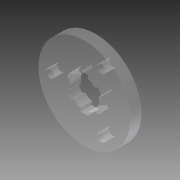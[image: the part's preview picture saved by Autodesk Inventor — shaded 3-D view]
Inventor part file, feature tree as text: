
AUTODESK INVENTOR PART (.ipt)
format: ipt  version: 2014 SP1 (Build 180222100, 222)  size: 126,976 bytes
history: native  units: in
note: dims shown in document units (in); Inventor stores cm internally (conversion verified against a paired STEP export)
features: reference x19, extrude x2, sketch x2
ambient origin geometry x8: Origin, YZ Plane, XZ Plane, XY Plane, X Axis, Y Axis, Z Axis, Center Point
bodies: Solid1 (feature_tree)
feature tree (23):
  extrude  "Extrusion1"  Depth=0.25in TaperAngle=0.0deg
  extrude  "Extrusion2"  Depth=1.0in TaperAngle=360.0deg
  sketch  "Sketch1"  dims[d0=2.0in d1=0.25in d2=0.0in]
  sketch  "Sketch2"  dims[d3=0.185in d4=1.1811in d6=360.0deg d8=0.75in d9=1.0in d10=0.0in]
  reference  "Reference1"
  reference  "Reference2"
  reference  "Reference3"
  reference  "Reference4"
  reference  "Reference5"
  reference  "Reference6"
  reference  "Reference7"
  reference  "Reference8"
  reference  "Reference9"
  reference  "Reference10"
  reference  "Reference11"
  reference  "Reference12"
  reference  "Reference13"
  reference  "Reference14"
  reference  "Reference15"
  reference  "Reference16"
  reference  "Reference17"
  reference  "Reference18"
  reference  "Reference19"
